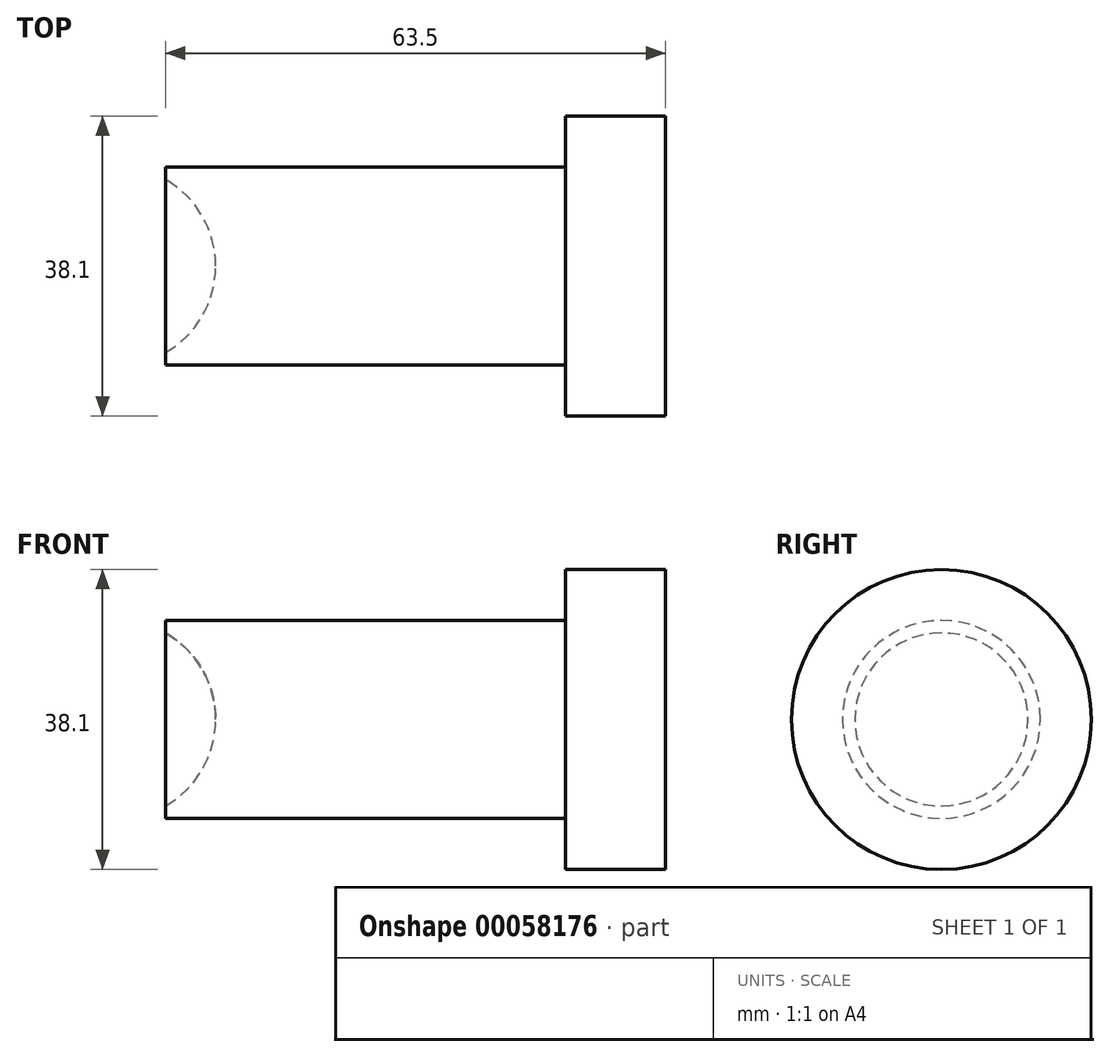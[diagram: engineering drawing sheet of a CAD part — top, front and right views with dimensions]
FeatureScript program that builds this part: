
annotation { "Feature Type Name" : "Feature", "Feature Type Description" : "" }
export const myFeature = defineFeature(function(context is Context, id is Id, definition is map)
    precondition{}
    {
        {
            var Q0;
            Q0=qCreatedBy(makeId("Right.planeOp"),FACE);
            var sketch = newSketch(context, id + "F0", { "sketchPlane" : qUnion([Q0])});
            skCircle(sketch, "E0", {"center": v(0, 0) * mm, "radius": 19.05 * mm});
            skSolve(sketch);
        }
        {
            var Q0;
            Q0 = qSketchRegion(id + "F0", true);
            extrude(context, id + "F1", {"entities" : qUnion([Q0]), "depth" : 12.7 * mm});
        }
        {
            var Q0;
            Q0=makeQuery(id+"F1.opExtrude","CAP_FACE",FACE,{"disambiguationData":[OSD([sQuery(id+"F0.wireOp",EDGE,"E0")])],"isStart":true});
            var sketch = newSketch(context, id + "F2", { "sketchPlane" : qUnion([Q0])});
            skCircle(sketch, "E1", {"center": v(0, 0) * mm, "radius": 12.57 * mm});
            skSolve(sketch);
        }
        {
            var Q0;
            Q0 = qSketchRegion(id + "F2", true);
            extrude(context, id + "F3", {"entities" : qUnion([Q0]), "operationType" : NewBodyOperationType.ADD, "depth" : 50.8 * mm});
        }
        {
            var Q0;
            Q0=qCreatedBy(makeId("Front.planeOp"),FACE);
            var sketch = newSketch(context, id + "F4", { "sketchPlane" : qUnion([Q0])});
            skArc(sketch, "E2", {"start": v(-44.45, 0) * mm, "mid": v(-46.15, 6.35) * mm, "end": v(-50.8, 11) * mm});
            skLineSegment(sketch, "E3", {"start": v(-50.8, 11) * mm, "end": v(-50.8, 0) * mm});
            skLineSegment(sketch, "E4", {"start": v(-50.8, 0) * mm, "end": v(-44.45, 0) * mm});
            skLineSegment(sketch, "E5", {"start": v(-75.98, 0) * mm, "end": v(-57.15, 0) * mm});
            skSolve(sketch);
        }
        {
            var Q0;
            Q0 = qSketchRegion(id + "F4", true);
            var Q1;
            Q1=sQuery(id+"F4.wireOp",EDGE,"E5");
            revolve(context, id + "F5", {"operationType" : NewBodyOperationType.REMOVE, "entities" : qUnion([Q0]), "axis" : qUnion([Q1]), "revolveType" : RevolveType.ONE_DIRECTION, "oppositeDirection" : true, "angle" : 360 * degree});
        }
    });
